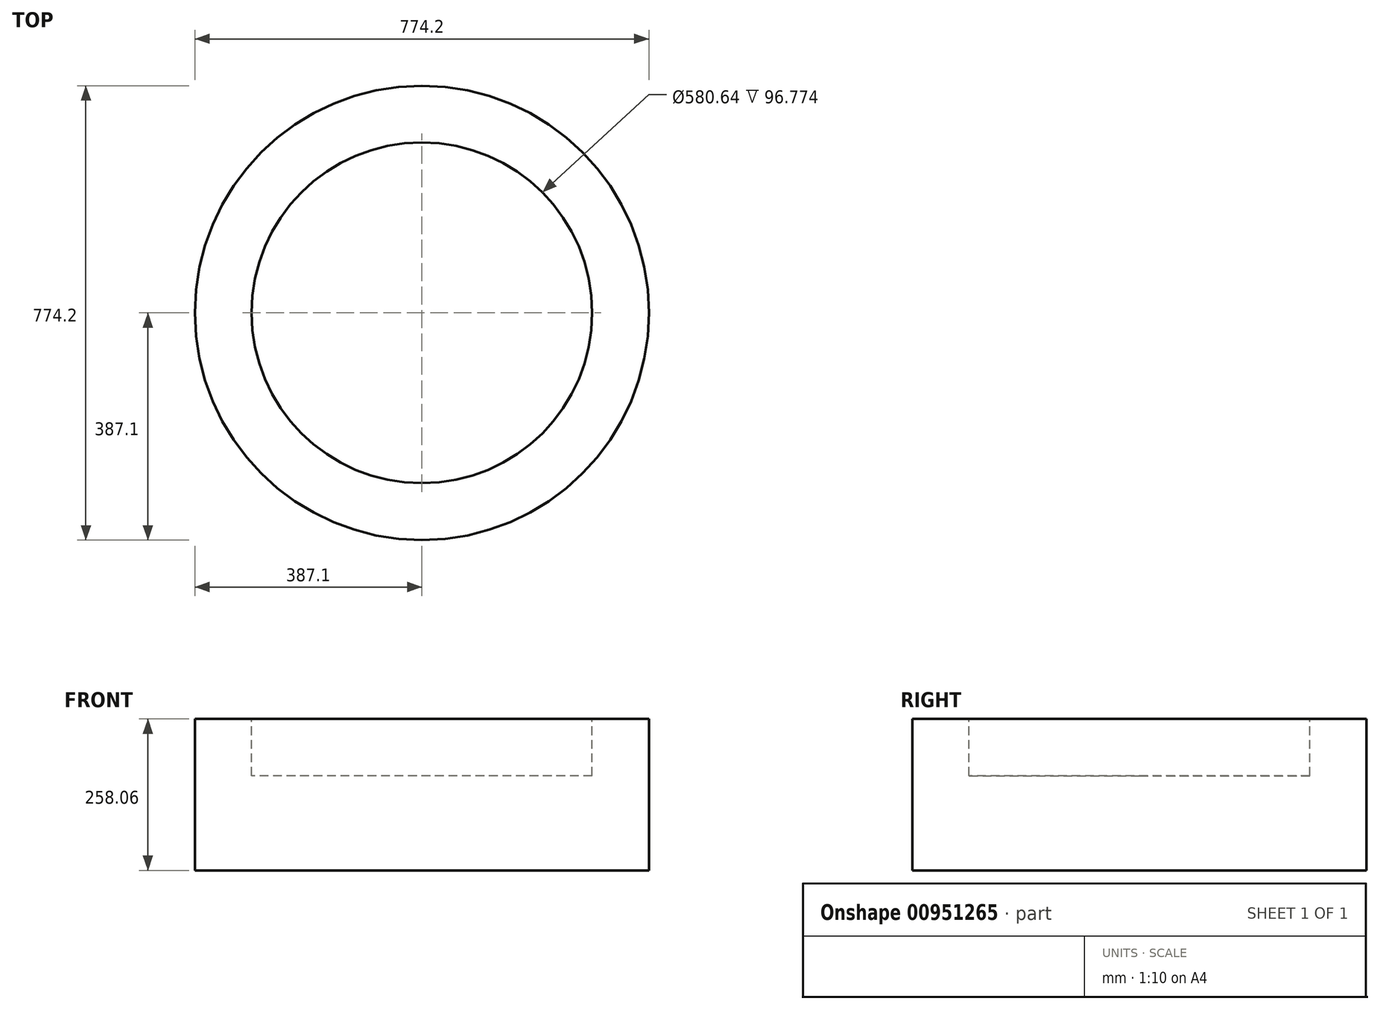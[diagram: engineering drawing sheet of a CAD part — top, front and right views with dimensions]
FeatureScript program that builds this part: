
annotation { "Feature Type Name" : "Feature", "Feature Type Description" : "" }
export const myFeature = defineFeature(function(context is Context, id is Id, definition is map)
    precondition{}
    {
        {
            var Q0;
            Q0=qCreatedBy(makeId("Top.planeOp"),FACE);
            var sketch = newSketch(context, id + "F0", { "sketchPlane" : qUnion([Q0])});
            skCircle(sketch, "E0", {"center": v(0, 0) * mm, "radius": 387.1 * mm});
            skSolve(sketch);
        }
        {
            var Q0;
            Q0 = qSketchRegion(id + "F0", true);
            extrude(context, id + "F1", {"entities" : qUnion([Q0]), "endBound" : BoundingType.SYMMETRIC, "depth" : 258.06 * mm, "offsetDistance" : 25.4 * mm});
        }
        {
            var Q0;
            Q0=makeQuery(id+"F1.opExtrude","CAP_FACE",FACE,{"disambiguationData":[OSD([sQuery(id+"F0.wireOp",EDGE,"E0")])],"isStart":false});
            var sketch = newSketch(context, id + "F2", { "sketchPlane" : qUnion([Q0])});
            skCircle(sketch, "E1", {"center": v(0, 0) * mm, "radius": 290.32 * mm});
            skSolve(sketch);
        }
        {
            var Q0;
            Q0 = qSketchRegion(id + "F2", true);
            extrude(context, id + "F3", {"entities" : qUnion([Q0]), "operationType" : NewBodyOperationType.REMOVE, "oppositeDirection" : true, "depth" : 96.77 * mm, "offsetDistance" : 25.4 * mm});
        }
    });
